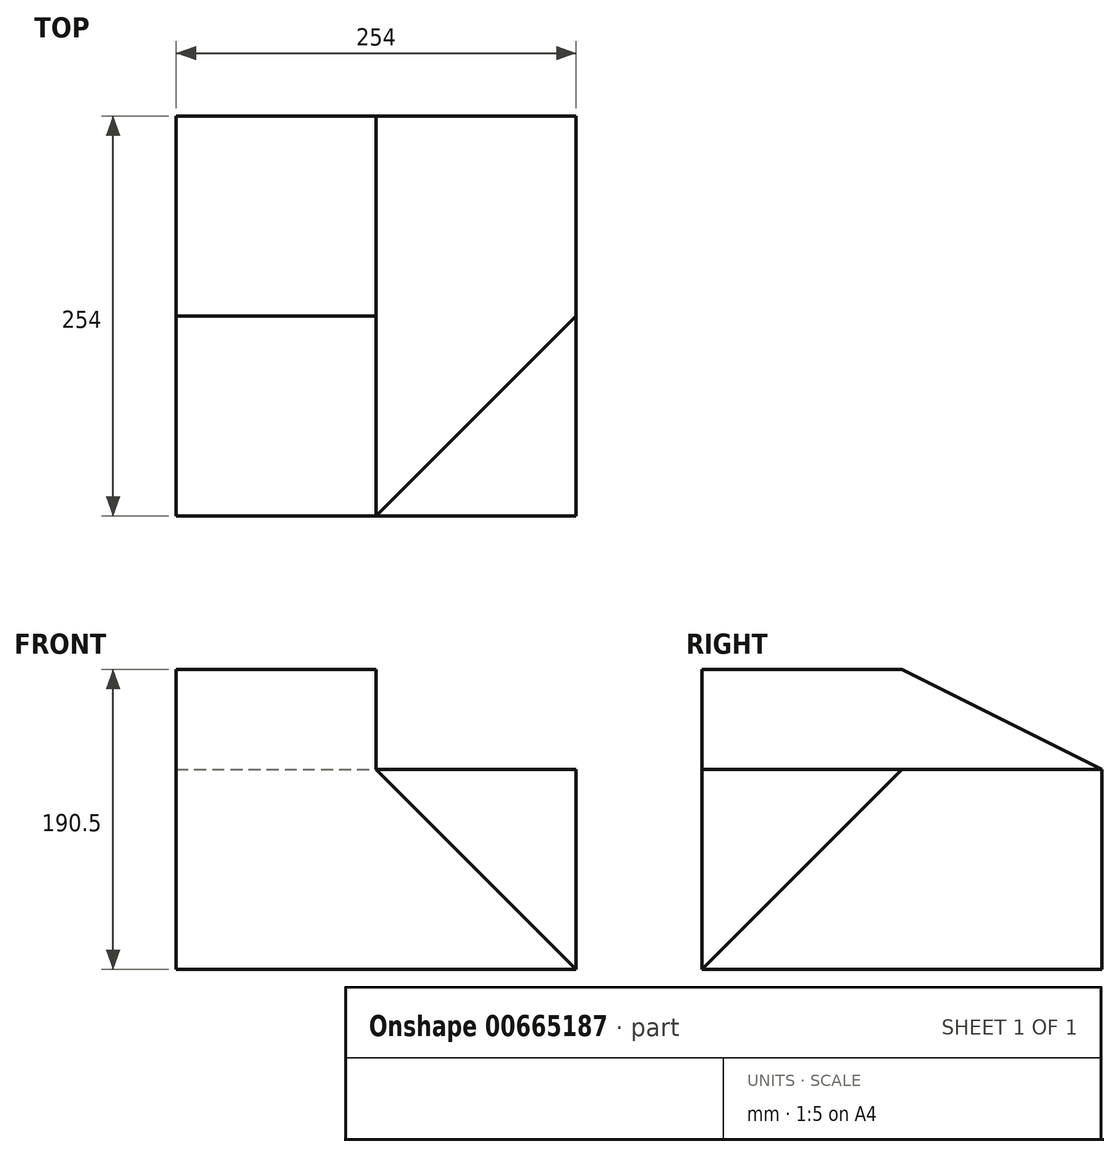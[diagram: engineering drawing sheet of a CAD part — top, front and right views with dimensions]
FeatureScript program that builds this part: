
annotation { "Feature Type Name" : "Feature", "Feature Type Description" : "" }
export const myFeature = defineFeature(function(context is Context, id is Id, definition is map)
    precondition{}
    {
        {
            var Q0;
            Q0=qCreatedBy(makeId("Top.planeOp"),FACE);
            var sketch = newSketch(context, id + "F0", { "sketchPlane" : qUnion([Q0])});
            skLineSegment(sketch, "E0", {"start": v(0, 0) * mm, "end": v(254, 0) * mm});
            skLineSegment(sketch, "E1", {"start": v(254, 0) * mm, "end": v(254, 254) * mm});
            skLineSegment(sketch, "E2", {"start": v(254, 254) * mm, "end": v(0, 254) * mm});
            skLineSegment(sketch, "E3", {"start": v(0, 254) * mm, "end": v(0, 0) * mm});
            skLineSegment(sketch, "E4", {"start": v(127, 254) * mm, "end": v(127, 0) * mm});
            skLineSegment(sketch, "E5", {"start": v(0, 127) * mm, "end": v(127, 127) * mm});
            skLineSegment(sketch, "E6", {"start": v(127, 0) * mm, "end": v(254, 127) * mm});
            skSolve(sketch);
        }
        {
            var Q0;
            {var subQ5=sQuery(id+"F0.wireOp",EDGE,"E5");Q0=makeQuery(id+"F0.imprint","IMPRINT",FACE,{"disambiguationData":[TD([[makeQuery(id+"F0.imprint","IMPRINT",EDGE,{"derivedFrom":subQ5}),-1.0]])]});}
            var Q1;
            {var subQ5=sQuery(id+"F0.wireOp",EDGE,"E5");Q1=makeQuery(id+"F0.imprint","IMPRINT",FACE,{"disambiguationData":[TD([[makeQuery(id+"F0.imprint","IMPRINT",EDGE,{"derivedFrom":subQ5}),1.0]])]});}
            extrude(context, id + "F1", {"entities" : qUnion([Q0, Q1]), "depth" : 190.5 * mm, "offsetDistance" : 25.4 * mm});
        }
        {
            var Q0;
            {var subQ0=sQuery(id+"F0.wireOp",EDGE,"E6");Q0=makeQuery(id+"F0.imprint","IMPRINT",FACE,{"disambiguationData":[TD([[makeQuery(id+"F0.imprint","IMPRINT",EDGE,{"derivedFrom":subQ0}),1.0]])]});}
            var Q1;
            {var subQ3=sQuery(id+"F0.wireOp",EDGE,"E6");Q1=makeQuery(id+"F0.imprint","IMPRINT",FACE,{"disambiguationData":[TD([[makeQuery(id+"F0.imprint","IMPRINT",EDGE,{"derivedFrom":subQ3}),-1.0]])]});}
            extrude(context, id + "F2", {"entities" : qUnion([Q0, Q1]), "operationType" : NewBodyOperationType.ADD, "depth" : 127 * mm, "offsetDistance" : 25.4 * mm});
        }
        {
            var Q0;
            Q0=makeQuery(id+"F1.opExtrude","SWEPT_FACE",FACE,{"disambiguationData":[OSD([sQuery(id+"F0.wireOp",EDGE,"E4")])]});
            var sketch = newSketch(context, id + "F3", { "sketchPlane" : qUnion([Q0])});
            skLineSegment(sketch, "E7", {"start": v(127, 190.5) * mm, "end": v(254, 127) * mm});
            skLineSegment(sketch, "E8", {"start": v(254, 127) * mm, "end": v(254, 190.5) * mm});
            skLineSegment(sketch, "E9", {"start": v(254, 190.5) * mm, "end": v(127, 190.5) * mm});
            skSolve(sketch);
        }
        {
            var Q0;
            Q0=makeQuery(id+"F3.imprint","IMPRINT",FACE,{"disambiguationData":[TD([[makeQuery(id+"F3.imprint","IMPRINT",EDGE,{"derivedFrom":sQuery(id+"F3.wireOp",EDGE,"E7")}),1.0]])]});
            extrude(context, id + "F4", {"entities" : qUnion([Q0]), "operationType" : NewBodyOperationType.REMOVE, "oppositeDirection" : true, "depth" : 127 * mm, "offsetDistance" : 25.4 * mm});
        }
        {
            var Q0;
            Q0=makeQuery(id+"F2.opExtrude","CAP_EDGE",EDGE,{"disambiguationData":[OSD([sQuery(id+"F0.wireOp",EDGE,"E1")])],"isStart":false});
            cPoint(context, id + "F5", {"entities" : qUnion([Q0]), "parameter" : 0.5});
        }
        {
            var Q0;
            Q0 = qCreatedBy(id + "F5" ,VERTEX);
            var Q1;
            Q1=sQuery(id+"F0.wireOp",VERTEX,"E1.start");
            var Q2;
            Q2=makeQuery(id+"F2.opExtrude","CAP_VERTEX",VERTEX,{"disambiguationData":[OSD([sQuery(id+"F0.wireOp",EDGE,"E0"),sQuery(id+"F0.wireOp",EDGE,"E4"),sQuery(id+"F0.wireOp",EDGE,"E6")])],"isStart":false});
            cPlane(context, id + "F6", {"entities" : qUnion([Q0, Q1, Q2]), "cplaneType" : CPlaneType.THREE_POINT, "offset" : 25.4 * mm, "width" : 152.4 * mm, "height" : 152.4 * mm});
        }
        {
            var Q0;
            Q0=qCreatedBy(id+"F6.planeOp",FACE);
            var sketch = newSketch(context, id + "F7", { "sketchPlane" : qUnion([Q0])});
            skLineSegment(sketch, "E10", {"start": v(207.4, 179.6) * mm, "end": v(51.85, 89.8) * mm});
            skLineSegment(sketch, "E11", {"start": v(207.4, 179.6) * mm, "end": v(207.4, 0) * mm});
            skLineSegment(sketch, "E12", {"start": v(207.4, 0) * mm, "end": v(51.85, 89.8) * mm});
            skSolve(sketch);
        }
        {
            var Q0;
            Q0 = qSketchRegion(id + "F7", true);
            extrude(context, id + "F8", {"entities" : qUnion([Q0]), "operationType" : NewBodyOperationType.REMOVE, "depth" : 76.2 * mm, "offsetDistance" : 25.4 * mm});
        }
    });
